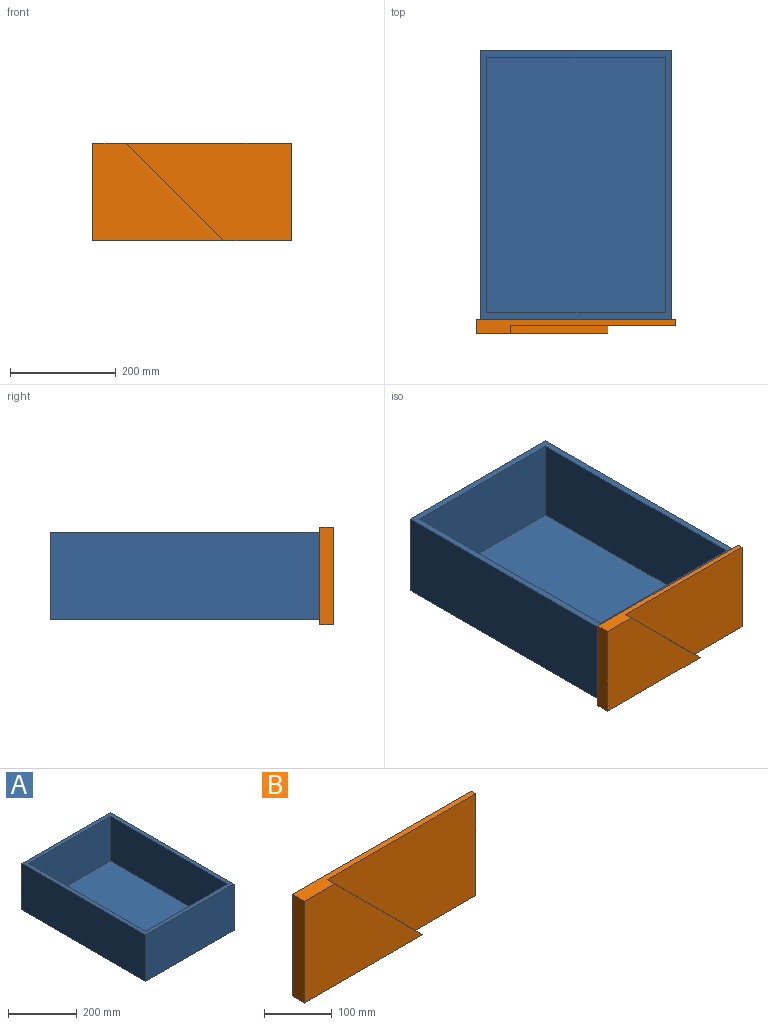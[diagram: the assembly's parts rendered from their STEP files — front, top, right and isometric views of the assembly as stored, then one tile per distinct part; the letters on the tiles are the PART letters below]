
ASSEMBLY  parts=2 mates=1
PART A: 11 faces, bbox 362x508x165.1 mm
  f0: plane 508x165.1mm, normal (-1,0,0), area 83870.8mm2, adj f1,f3,f4,f5
  f1: plane 361.95x165.1mm, normal (0,-1,0), area 59757.9mm2, adj f0,f2,f4,f5
  f2: plane 508x165.1mm, normal (1,0,0), area 83870.8mm2, adj f1,f3,f4,f5
  f3: plane 361.95x165.1mm, normal (0,1,0), area 59757.9mm2, adj f0,f2,f4,f5
  f4: plane 508x361.95mm, normal (0,0,1), area 21451.6mm2, adj f0,f1,f2,f3,f7,f8,f9,f10
  f5: plane 508x361.95mm, normal (0,0,-1), area 183870.6mm2, adj f0,f1,f2,f3
  f6: plane 482.6x336.55mm, normal (0,0,1), area 162419mm2, adj f7,f8,f9,f10
  f7: plane 482.6x158.75mm, normal (1,0,0), area 76612.8mm2, adj f4,f6,f8,f10
  f8: plane 336.55x158.75mm, normal (0,1,0), area 53427.3mm2, adj f4,f6,f7,f9
  f9: plane 482.6x158.75mm, normal (-1,0,0), area 76612.8mm2, adj f4,f6,f8,f10
  f10: plane 336.55x158.75mm, normal (0,-1,0), area 53427.3mm2, adj f4,f6,f7,f9
PART B: 8 faces, bbox 374.7x25.4x184.2 mm
  f0: plane 184.15x10.16mm, normal (1,0,0), area 1871mm2, adj f1,f3,f5,f7
  f1: plane 374.65x25.4mm, normal (0,0,1), area 4774.2mm2, adj f0,f2,f4,f5,f6,f7
  f2: plane 184.15x25.4mm, normal (-1,0,0), area 4677.4mm2, adj f1,f3,f4,f5
  f3: plane 374.65x25.4mm, normal (0,0,-1), area 7580.6mm2, adj f0,f2,f4,f5,f6,f7
  f4: plane 247.65x184.15mm, normal (0,-1,0), area 28649.1mm2, adj f1,f2,f3,f6
  f5: plane 374.65x184.15mm, normal (0,1,0), area 68991.8mm2, adj f0,f1,f2,f3
  f6: plane 184.15x184.15mm, normal (0.71,0,0.71), area 3968.9mm2, adj f1,f3,f4,f7
  f7: plane 311.15x184.15mm, normal (0,-1,0), area 40342.7mm2, adj f0,f1,f3,f6
PLACE A t=(-97.78,-103.22,71.57)mm fixed
PLACE B t=(-104.13,-103.22,62.04)mm
MATE fastened B.f5 <-> A.f1  axis (0,1,0) through (83.2,-103.22,154.12)mm
